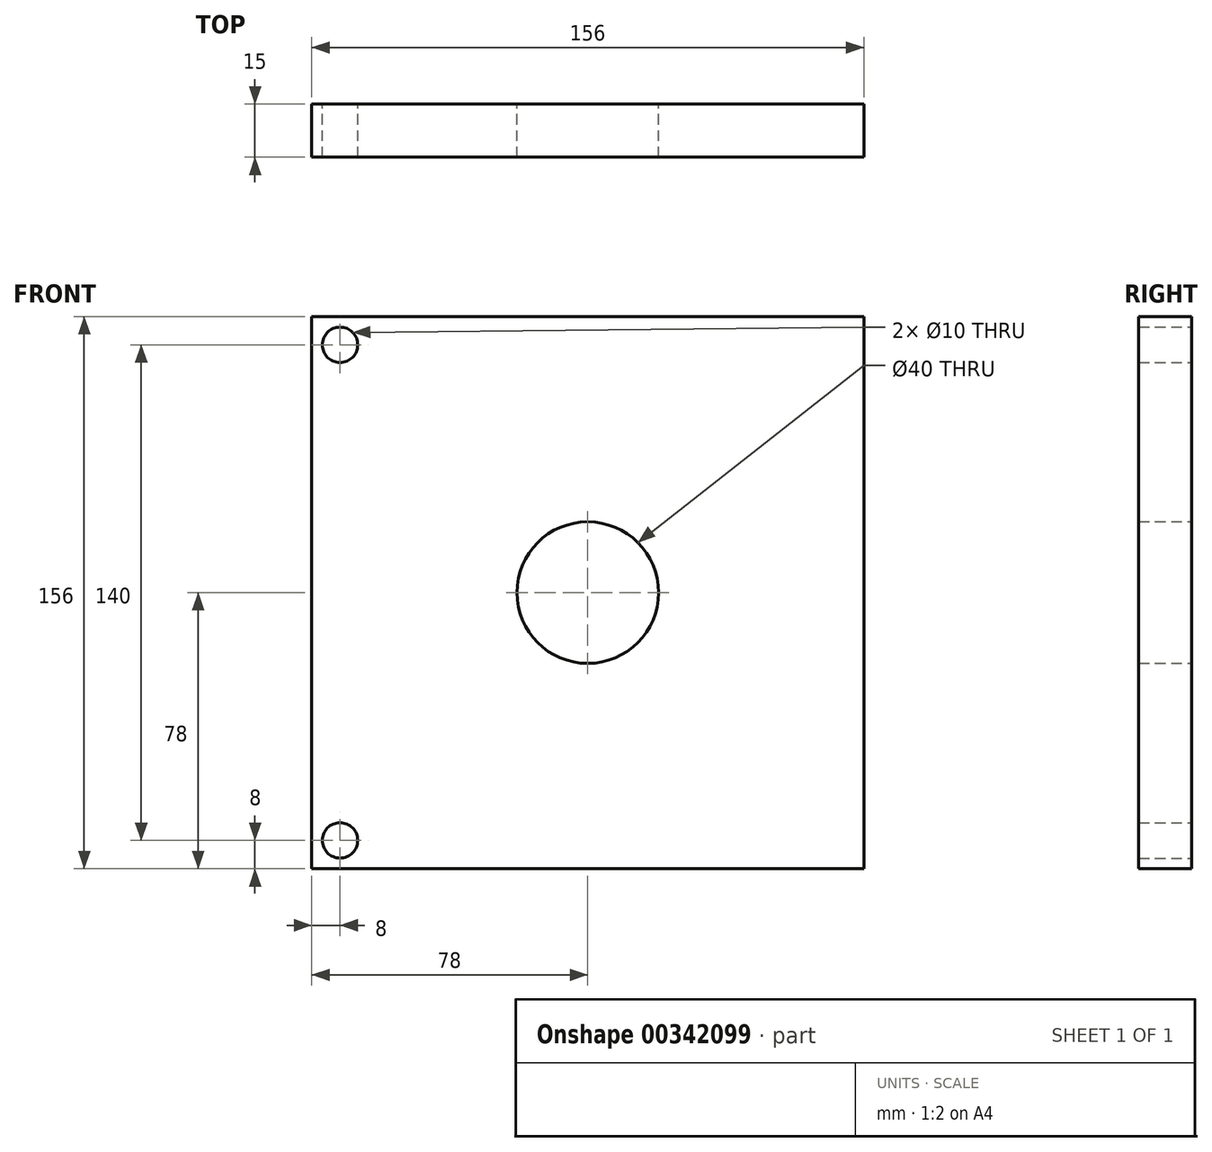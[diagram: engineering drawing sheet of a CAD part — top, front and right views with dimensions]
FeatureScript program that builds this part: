
annotation { "Feature Type Name" : "Feature", "Feature Type Description" : "" }
export const myFeature = defineFeature(function(context is Context, id is Id, definition is map)
    precondition{}
    {
        {
            var Q0;
            Q0=qCreatedBy(makeId("Front.planeOp"),FACE);
            var sketch = newSketch(context, id + "F0", { "sketchPlane" : qUnion([Q0])});
            skLineSegment(sketch, "E0.bottom", {"start": v(-78, -78) * mm, "end": v(78, -78) * mm});
            skLineSegment(sketch, "E0.top", {"start": v(-78, 78) * mm, "end": v(78, 78) * mm});
            skLineSegment(sketch, "E0.left", {"start": v(-78, -78) * mm, "end": v(-78, 78) * mm});
            skLineSegment(sketch, "E0.right", {"start": v(78, -78) * mm, "end": v(78, 78) * mm});
            skPoint(sketch, "E0.middle", {"position": v(0, 0) * mm});
            skLineSegment(sketch, "E1", {"start": v(-78, -78) * mm, "end": v(-73, -78) * mm});
            skLineSegment(sketch, "E2.MirrorCS", {"start": v(-78, 78) * mm, "end": v(-73, 78) * mm});
            skLineSegment(sketch, "E3.MirrorCS", {"start": v(-78, 78) * mm, "end": v(-78, -78) * mm});
            skLineSegment(sketch, "E4.MirrorCS", {"start": v(78, 78) * mm, "end": v(73, 78) * mm});
            skLineSegment(sketch, "E5.MirrorCS", {"start": v(78, -78) * mm, "end": v(73, -78) * mm});
            skLineSegment(sketch, "E6.MirrorCS", {"start": v(78, 78) * mm, "end": v(-78, 78) * mm});
            skLineSegment(sketch, "E7.MirrorCS", {"start": v(78, 78) * mm, "end": v(78, -78) * mm});
            skLineSegment(sketch, "E8.MirrorCS", {"start": v(78, -78) * mm, "end": v(-78, -78) * mm});
            skCircle(sketch, "E9", {"center": v(0, 0) * mm, "radius": 20 * mm});
            skCircle(sketch, "E10", {"center": v(-70, 70) * mm, "radius": 5 * mm});
            skLineSegment(sketch, "E11", {"start": v(-70, 70) * mm, "end": v(70, 70) * mm, "construction": true});
            skLineSegment(sketch, "E12", {"start": v(70, 70) * mm, "end": v(70, -70) * mm, "construction": true});
            skLineSegment(sketch, "E13", {"start": v(70, -70) * mm, "end": v(-70, -70) * mm, "construction": true});
            skLineSegment(sketch, "E14", {"start": v(-70, -70) * mm, "end": v(-70, 70) * mm, "construction": true});
            skCircle(sketch, "E15", {"center": v(-70, -70) * mm, "radius": 5 * mm});
            skSolve(sketch);
        }
        {
            var Q0;
            Q0=qSketchRegion(id+"F0",true);
            extrude(context, id + "F1", {"entities" : qUnion([Q0]), "depth" : 15 * mm});
        }
    });
